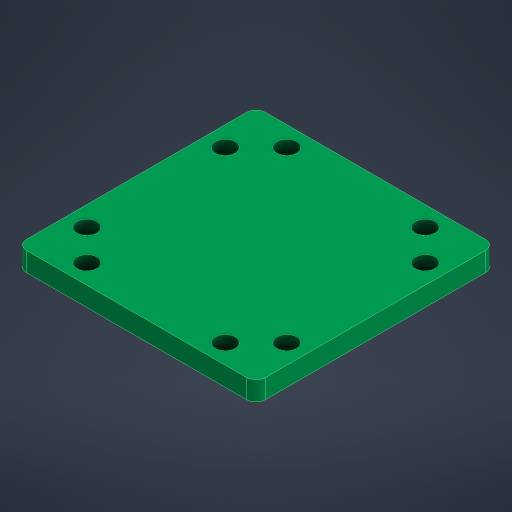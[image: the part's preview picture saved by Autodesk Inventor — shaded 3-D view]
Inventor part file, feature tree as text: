
AUTODESK INVENTOR PART (.ipt)
format: ipt  version: 2023.4 (Build 274418000, 418)  size: 183,808 bytes
history: native  units: mm
features: other x3, sketch x1, plane x1, extrude x1, reference x1
ambient origin geometry x8: Origin, YZ Plane, XZ Plane, XY Plane, X Axis, Y Axis, Z Axis, Center Point
bodies: Solid1 (feature_tree)
feature tree (7):
  sketch  "Sketch1"  dims[d0=4.0mm d1=0.0mm]
  plane  "Work Plane1"
  extrude  "Extrusion1"  [1 undecoded]
  reference  "Reference1"
  other  "<path>\Projects\Project Protocube\Protocube\CAD, STL, OBJ Files\1 CAD\Cube 1x1 V5.iam"
  other  "Cube 1x1 V5.iam"
  other  "Cube 1x1 Top V5 Closed Slotted:1"
note: 1 required parameter value undecoded (feature->parameter linkage not recoverable at this tier; creation-order binding heuristic only, values carry confidence <= 0.55)
note: 1 file-system path scrubbed to <path> (originals preserved in map.json)
